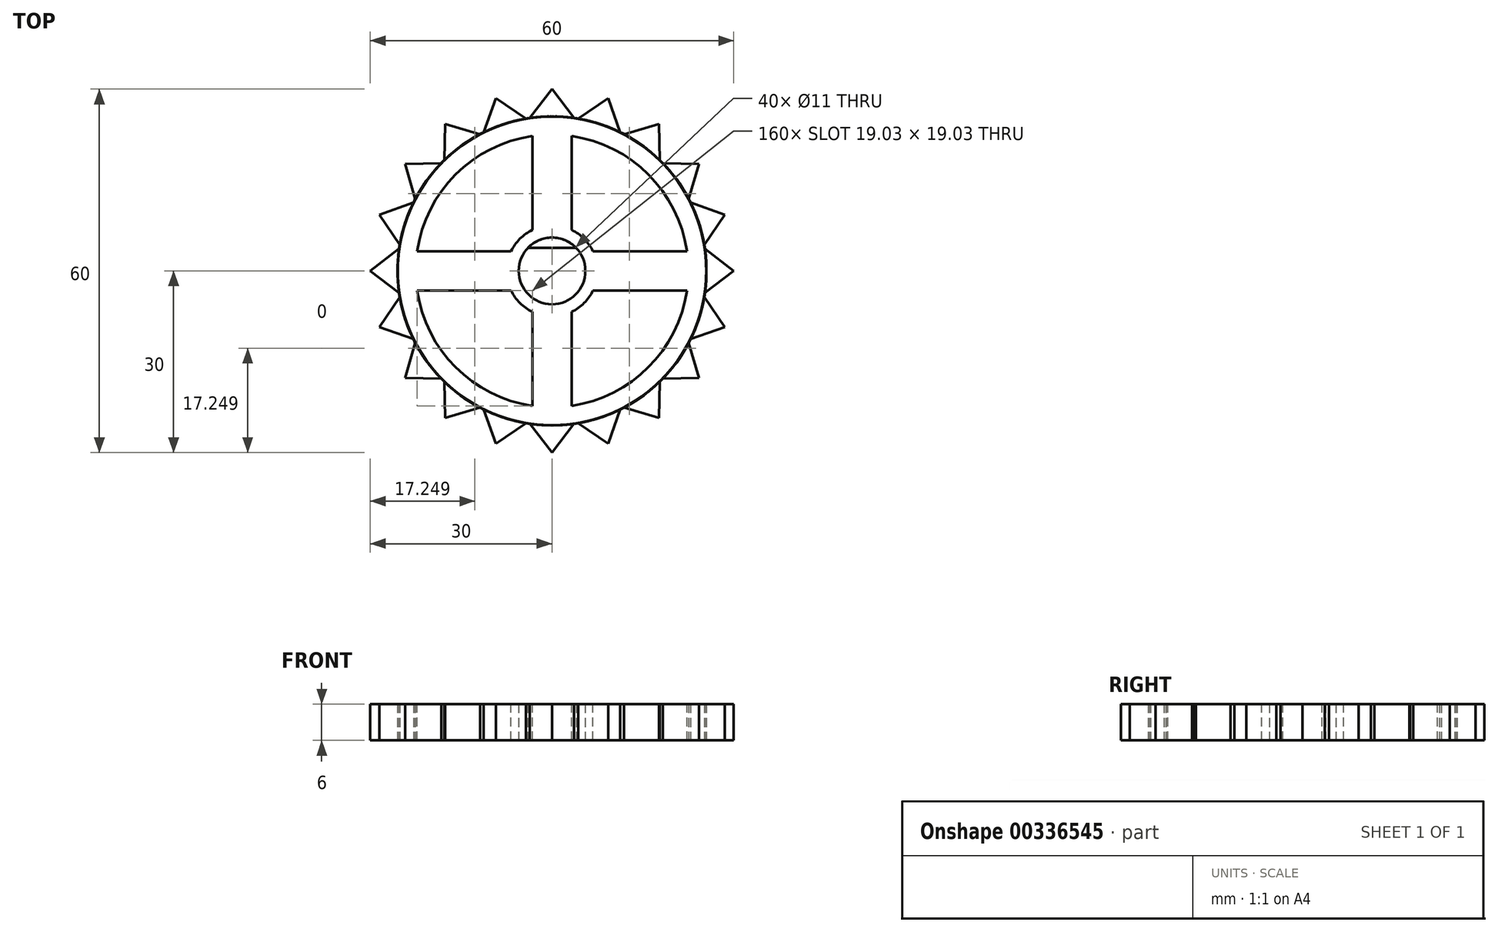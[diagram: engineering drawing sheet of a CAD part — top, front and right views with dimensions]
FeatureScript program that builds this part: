
annotation { "Feature Type Name" : "Feature", "Feature Type Description" : "" }
export const myFeature = defineFeature(function(context is Context, id is Id, definition is map)
    precondition{}
    {
        {
            var Q0;
            Q0=qCreatedBy(makeId("Top.planeOp"),FACE);
            var sketch = newSketch(context, id + "F0", { "sketchPlane" : qUnion([Q0])});
            skCircle(sketch, "E0", {"center": v(0, 0) * mm, "radius": 5.5 * mm});
            skCircle(sketch, "E1", {"center": v(0, 0) * mm, "radius": 25.5 * mm});
            skCircle(sketch, "E2", {"center": v(0, 0) * mm, "radius": 30 * mm});
            skLineSegment(sketch, "E3", {"start": v(-4, 3.77) * mm, "end": v(4, 3.77) * mm});
            skLineSegment(sketch, "E4", {"start": v(0, 30) * mm, "end": v(-3.65, 25.24) * mm});
            skLineSegment(sketch, "E5", {"start": v(0, 30) * mm, "end": v(3.65, 25.24) * mm});
            skSolve(sketch);
        }
        {
            var Q0;
            {var subQ0=sQuery(id+"F0.wireOp",EDGE,"E3");var subQ1=sQuery(id+"F0.wireOp",EDGE,"E0");var subQ2=makeQuery(id+"F0.imprint","INTERSECT",VERTEX,{"disambiguationData":[OD(0.0)],"derivedFrom":[subQ1,subQ0]});Q0=makeQuery(id+"F0.imprint","IMPRINT",FACE,{"disambiguationData":[TD([[makeQuery(id+"F0.imprint","IMPRINT",EDGE,{"disambiguationData":[TD([[subQ2,1.0]])],"derivedFrom":subQ1}),-1.0]])]});}
            var Q1;
            {var subQ0=sQuery(id+"F0.wireOp",EDGE,"E4");Q1=makeQuery(id+"F0.imprint","IMPRINT",FACE,{"disambiguationData":[TD([[makeQuery(id+"F0.imprint","IMPRINT",EDGE,{"derivedFrom":subQ0}),1.0]])]});}
            extrude(context, id + "F1", {"entities" : qUnion([Q0, Q1]), "depth" : 6 * mm});
        }
        {
            var Q0;
            Q0=qCreatedBy(makeId("Right.planeOp"),FACE);
            var sketch = newSketch(context, id + "F2", { "sketchPlane" : qUnion([Q0])});
            skLineSegment(sketch, "E6", {"start": v(0, 0) * mm, "end": v(0, 18.83) * mm});
            skSolve(sketch);
        }
        {
            var Q0;
            Q0=makeQuery(id+"F1.opExtrude","SWEPT_BODY",BODY,{"disambiguationData":[OSD([sQuery(id+"F0.wireOp",EDGE,"E0"),sQuery(id+"F0.wireOp",EDGE,"E1"),sQuery(id+"F0.wireOp",EDGE,"E4"),sQuery(id+"F0.wireOp",EDGE,"E5")])]});
            var Q1;
            Q1=sQuery(id+"F2.wireOp",EDGE,"E6");
            circularPattern(context, id + "F3", {"entities" : qUnion([Q0]), "axis" : qUnion([Q1]), "angle" : 360 * degree, "instanceCount" : 20, "equalSpace" : true});
        }
        {
            var Q0;
            {var subQ0=sQuery(id+"F0.wireOp",EDGE,"E3");Q0=makeQuery(id+"F0.imprint","IMPRINT",FACE,{"disambiguationData":[TD([[makeQuery(id+"F0.imprint","IMPRINT",EDGE,{"derivedFrom":subQ0}),1.0]])]});}
            extrude(context, id + "F4", {"entities" : qUnion([Q0]), "depth" : 6 * mm});
        }
        {
            var Q0;
            Q0=makeQuery(id+"F3.opPattern","COPY",FACE,{"derivedFrom":makeQuery(id+"F1.opExtrude","CAP_FACE",FACE,{"disambiguationData":[OSD([sQuery(id+"F0.wireOp",EDGE,"E0"),sQuery(id+"F0.wireOp",EDGE,"E1"),sQuery(id+"F0.wireOp",EDGE,"E4"),sQuery(id+"F0.wireOp",EDGE,"E5")])],"isStart":false}),"instanceName":"16"});
            var sketch = newSketch(context, id + "F5", { "sketchPlane" : qUnion([Q0])});
            skCircle(sketch, "E7", {"center": v(0, 0) * mm, "radius": 7.5 * mm});
            skCircle(sketch, "E8", {"center": v(0, 0) * mm, "radius": 22.5 * mm});
            skLineSegment(sketch, "E9", {"start": v(-22.27, 3.24) * mm, "end": v(-6.77, 3.24) * mm});
            skLineSegment(sketch, "E10", {"start": v(-22.27, -3.24) * mm, "end": v(-6.77, -3.24) * mm});
            skLineSegment(sketch, "E11", {"start": v(-3.24, 6.77) * mm, "end": v(-3.24, 22.27) * mm});
            skLineSegment(sketch, "E12", {"start": v(3.24, 6.77) * mm, "end": v(3.24, 22.27) * mm});
            skLineSegment(sketch, "E13", {"start": v(6.77, 3.24) * mm, "end": v(22.27, 3.24) * mm});
            skLineSegment(sketch, "E14", {"start": v(6.77, -3.24) * mm, "end": v(22.27, -3.24) * mm});
            skLineSegment(sketch, "E15", {"start": v(-3.24, -6.77) * mm, "end": v(-3.24, -22.27) * mm});
            skLineSegment(sketch, "E16", {"start": v(3.24, -6.77) * mm, "end": v(3.24, -22.27) * mm});
            skSolve(sketch);
        }
        {
            var Q0;
            {var subQ0=sQuery(id+"F5.wireOp",EDGE,"E12");Q0=makeQuery(id+"F5.imprint","IMPRINT",FACE,{"disambiguationData":[TD([[makeQuery(id+"F5.imprint","IMPRINT",EDGE,{"derivedFrom":subQ0}),-1.0]])]});}
            var Q1;
            {var subQ0=sQuery(id+"F5.wireOp",EDGE,"E10");Q1=makeQuery(id+"F5.imprint","IMPRINT",FACE,{"disambiguationData":[TD([[makeQuery(id+"F5.imprint","IMPRINT",EDGE,{"derivedFrom":subQ0}),-1.0]])]});}
            var Q2;
            {var subQ0=sQuery(id+"F5.wireOp",EDGE,"E14");Q2=makeQuery(id+"F5.imprint","IMPRINT",FACE,{"disambiguationData":[TD([[makeQuery(id+"F5.imprint","IMPRINT",EDGE,{"derivedFrom":subQ0}),-1.0]])]});}
            var Q3;
            {var subQ0=sQuery(id+"F5.wireOp",EDGE,"E9");Q3=makeQuery(id+"F5.imprint","IMPRINT",FACE,{"disambiguationData":[TD([[makeQuery(id+"F5.imprint","IMPRINT",EDGE,{"derivedFrom":subQ0}),1.0]])]});}
            extrude(context, id + "F6", {"entities" : qUnion([Q0, Q1, Q2, Q3]), "operationType" : NewBodyOperationType.REMOVE, "oppositeDirection" : true, "depth" : 6 * mm});
        }
    });
